# Revit family: assa_abloy_sl500_oc_03
name_source: partatom
category: Doors
units: mm (PartAtom-declared; Revit-internal decimal feet)

## family parameters
Always vertical = Yes
Cut with Voids When Loaded = No
Host = Wall
OmniClass Number = 23.30.10.00
OmniClass Title = Doors
Room Calculation Point = No
Shared = No

## types (5) — shared parameters
Analytic Construction = <None>
BIMobject category = Sliding Doors
Bottom Profile Height = Fix Leaf : 0'4''
Brass Polished Finish = Brass, Polished
Brass Satin Finish = Brass, Satin
Clear Anodized = Clear Anodized
Dark Bronze Anodized = Dark Bronze Anodized
Date of publishing = 2015-02-23
Depth = 0.00
Disclaimer = Consult product specification for sensors to comply with ANSI A156.10.
Edition number = 1
Fixed Leaf Bottom Profile Option 01 = Fix Leaf : 0'4''
Fixed Leaf Bottom Profile Option 02 = Fix Leaf : 0'7''
Fixed Leaf Bottom Profile Option 03 = Fix Leaf : 0'10''
Fixed Leaf Bottom Profile Option 04 = Fix Leaf : 0'12''
Frame Material = Clear Anodized
Function = Interior
Gap = 0' - 0 1/4"
Glass = Glass
Height = 7' - 6"
IFC Classification = Door
Leaf Height = 6' - 11 1/16"
Manufacturer name = Besam-North America
Material main = Aluminium
NBS Reference Code = 25-30-20-77
NBS Reference Description = Sliding Doorset Systems
Nominal height = 0.00
Nominal width = 0.00
Product SKU = SL500_OHC_Transom
Product data url = http://besam-na.bimobject.com
Product family = Sliding
Product group = Overhead Concealed
QR code = http://besam-na.bimobject.com
Rubber = Rubber, Black
Stainless Steel Polished Finish = Stainless Steel, Polished
Stainless Steel Satin Finish = Stainless Steel, Satin
UNSPSC Code = 301715
Uniclass 1.4 Code = L4133
Uniclass 1.4 Description = Sliding
Uniclass 2.0 Code = SS-25-30-20-77
Uniclass 2.0 Description = Sliding Doorset Systems
Wall Closure = By host
Weight Net (Kg) = 0

## per-type parameters (varying)
| type | Leaf Width | Rough Height | Rough Width | Thickness | Transom Height | Width |
| OC4-8 | 2' - 0 3/8" | 9' - 0 1/2" | 8' - 0 1/2" | 0' - 4 1/2" | 1' - 6 1/4" | 8' - 0" |
| OC4-10 | 2' - 6 3/8" | 9' - 0" | 10' - 0 1/2" | 0' - 6" | 1' - 5 3/4" | 10' - 0" |
| OC4-12 | 3' - 0 3/8" | 9' - 0 1/2" | 12' - 0 1/2" | 0' - 6" | 1' - 6 1/4" | 12' - 0" |
| OC4-14 | 3' - 6 3/8" | 9' - 0 1/2" | 14' - 0 1/2" | 0' - 6" | 1' - 6 1/4" | 14' - 0" |
| OC4-16 | 4' - 0 3/8" | 9' - 0 1/2" | 16' - 0 1/2" | 0' - 6" | 1' - 6 1/4" | 16' - 0" |

## geometry (parser evidence)
native form markers: Sweep x27
no freeform markers — native parametric forms only
